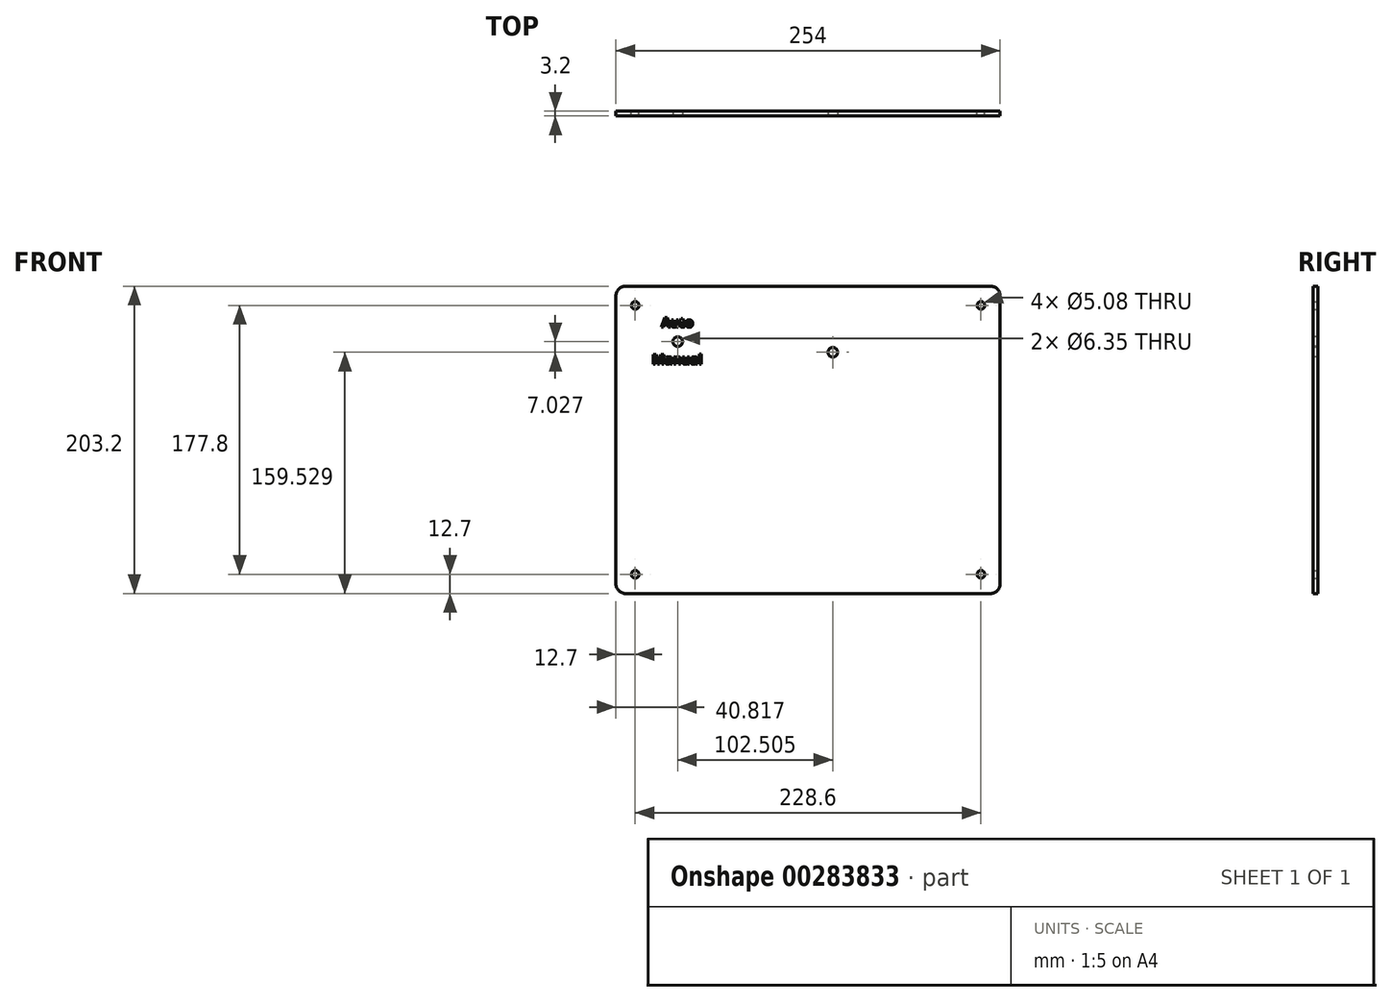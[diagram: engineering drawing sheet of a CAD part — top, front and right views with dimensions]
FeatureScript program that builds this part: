
annotation { "Feature Type Name" : "Feature", "Feature Type Description" : "" }
export const myFeature = defineFeature(function(context is Context, id is Id, definition is map)
    precondition{}
    {
        {
            var Q0;
            Q0=qCreatedBy(makeId("Front.planeOp"),FACE);
            var sketch = newSketch(context, id + "F0", { "sketchPlane" : qUnion([Q0])});
            skLineSegment(sketch, "E0.bottom", {"start": v(127, 101.6) * mm, "end": v(-127, 101.6) * mm});
            skLineSegment(sketch, "E0.top", {"start": v(127, -101.6) * mm, "end": v(-127, -101.6) * mm});
            skLineSegment(sketch, "E0.left", {"start": v(127, 101.6) * mm, "end": v(127, -101.6) * mm});
            skLineSegment(sketch, "E0.right", {"start": v(-127, 101.6) * mm, "end": v(-127, -101.6) * mm});
            skPoint(sketch, "E0.middle", {"position": v(0, 0) * mm});
            skLineSegment(sketch, "E1.bottom", {"start": v(-114.3, 88.9) * mm, "end": v(114.3, 88.9) * mm, "construction": true});
            skLineSegment(sketch, "E1.top", {"start": v(-114.3, -88.9) * mm, "end": v(114.3, -88.9) * mm, "construction": true});
            skLineSegment(sketch, "E1.left", {"start": v(-114.3, 88.9) * mm, "end": v(-114.3, -88.9) * mm, "construction": true});
            skLineSegment(sketch, "E1.right", {"start": v(114.3, 88.9) * mm, "end": v(114.3, -88.9) * mm, "construction": true});
            skCircle(sketch, "E2", {"center": v(-114.3, 88.9) * mm, "radius": 2.54 * mm});
            skCircle(sketch, "E3", {"center": v(114.3, 88.9) * mm, "radius": 2.54 * mm});
            skCircle(sketch, "E4", {"center": v(114.3, -88.9) * mm, "radius": 2.54 * mm});
            skCircle(sketch, "E5", {"center": v(-114.3, -88.9) * mm, "radius": 2.54 * mm});
            skSolve(sketch);
        }
        {
            var Q0;
            Q0 = qSketchRegion(id + "F0", true);
            extrude(context, id + "F1", {"entities" : qUnion([Q0]), "depth" : 3.17 * mm});
        }
        {
            var Q0;
            Q0=makeQuery(id+"F1.opExtrude","SWEPT_EDGE",EDGE,{"disambiguationData":[OSD([sQuery(id+"F0.wireOp",EDGE,"E0.top"),sQuery(id+"F0.wireOp",EDGE,"E0.right")])]});
            var Q1;
            Q1=makeQuery(id+"F1.opExtrude","SWEPT_EDGE",EDGE,{"disambiguationData":[OSD([sQuery(id+"F0.wireOp",EDGE,"E0.top"),sQuery(id+"F0.wireOp",EDGE,"E0.left")])]});
            var Q2;
            Q2=makeQuery(id+"F1.opExtrude","SWEPT_EDGE",EDGE,{"disambiguationData":[OSD([sQuery(id+"F0.wireOp",EDGE,"E0.bottom"),sQuery(id+"F0.wireOp",EDGE,"E0.left")])]});
            var Q3;
            Q3=makeQuery(id+"F1.opExtrude","SWEPT_EDGE",EDGE,{"disambiguationData":[OSD([sQuery(id+"F0.wireOp",EDGE,"E0.bottom"),sQuery(id+"F0.wireOp",EDGE,"E0.right")])]});
            fillet(context, id + "F2", {"entities" : qUnion([Q0, Q1, Q2, Q3]), "radius" : 6.35 * mm, "tangentPropagation" : true, "allowEdgeOverflow" : false});
        }
        {
            var Q0;
            Q0=makeQuery(id+"F1.opExtrude","CAP_FACE",FACE,{"disambiguationData":[OSD([sQuery(id+"F0.wireOp",EDGE,"E0.bottom"),sQuery(id+"F0.wireOp",EDGE,"E0.top"),sQuery(id+"F0.wireOp",EDGE,"E0.left"),sQuery(id+"F0.wireOp",EDGE,"E0.right"),sQuery(id+"F0.wireOp",EDGE,"E2"),sQuery(id+"F0.wireOp",EDGE,"E3"),sQuery(id+"F0.wireOp",EDGE,"E4"),sQuery(id+"F0.wireOp",EDGE,"E5")])],"isStart":false});
            var sketch = newSketch(context, id + "F3", { "sketchPlane" : qUnion([Q0])});
            skCircle(sketch, "E6", {"center": v(-86.18, 64.96) * mm, "radius": 3.18 * mm});
            skCircle(sketch, "E7", {"center": v(16.32, 57.93) * mm, "radius": 3.18 * mm});
            skSolve(sketch);
        }
        {
            var Q0;
            Q0 = qSketchRegion(id + "F3", true);
            extrude(context, id + "F4", {"entities" : qUnion([Q0]), "operationType" : NewBodyOperationType.REMOVE, "endBound" : BoundingType.UP_TO_NEXT, "oppositeDirection" : true, "depth" : 25.4 * mm});
        }
        {
            var Q0;
            Q0=makeQuery(id+"F1.opExtrude","CAP_FACE",FACE,{"disambiguationData":[OSD([sQuery(id+"F0.wireOp",EDGE,"E0.bottom"),sQuery(id+"F0.wireOp",EDGE,"E0.top"),sQuery(id+"F0.wireOp",EDGE,"E0.left"),sQuery(id+"F0.wireOp",EDGE,"E0.right"),sQuery(id+"F0.wireOp",EDGE,"E2"),sQuery(id+"F0.wireOp",EDGE,"E3"),sQuery(id+"F0.wireOp",EDGE,"E4"),sQuery(id+"F0.wireOp",EDGE,"E5")])],"isStart":false});
            var sketch = newSketch(context, id + "F5", { "sketchPlane" : qUnion([Q0])});
            skText(sketch, "E8", { "text": "Auto", "fontName": "OpenSans-Bold.ttf"});
            skText(sketch, "E9", { "text": "Manual", "fontName": "OpenSans-Bold.ttf"});
            const initialGuessF5  = {"E8": [-0.09705, 0.07449, 1, 0, 0.00635], "E9": [-0.10304, 0.05008, 1, 0, 0.00635]};
            skSetInitialGuess(sketch, initialGuessF5);
            skSolve(sketch);
        }
        {
            var Q0;
            Q0 = qSketchRegion(id + "F5", true);
            extrude(context, id + "F6", {"entities" : qUnion([Q0]), "operationType" : NewBodyOperationType.ADD, "depth" : 0.03 * mm});
        }
    });
